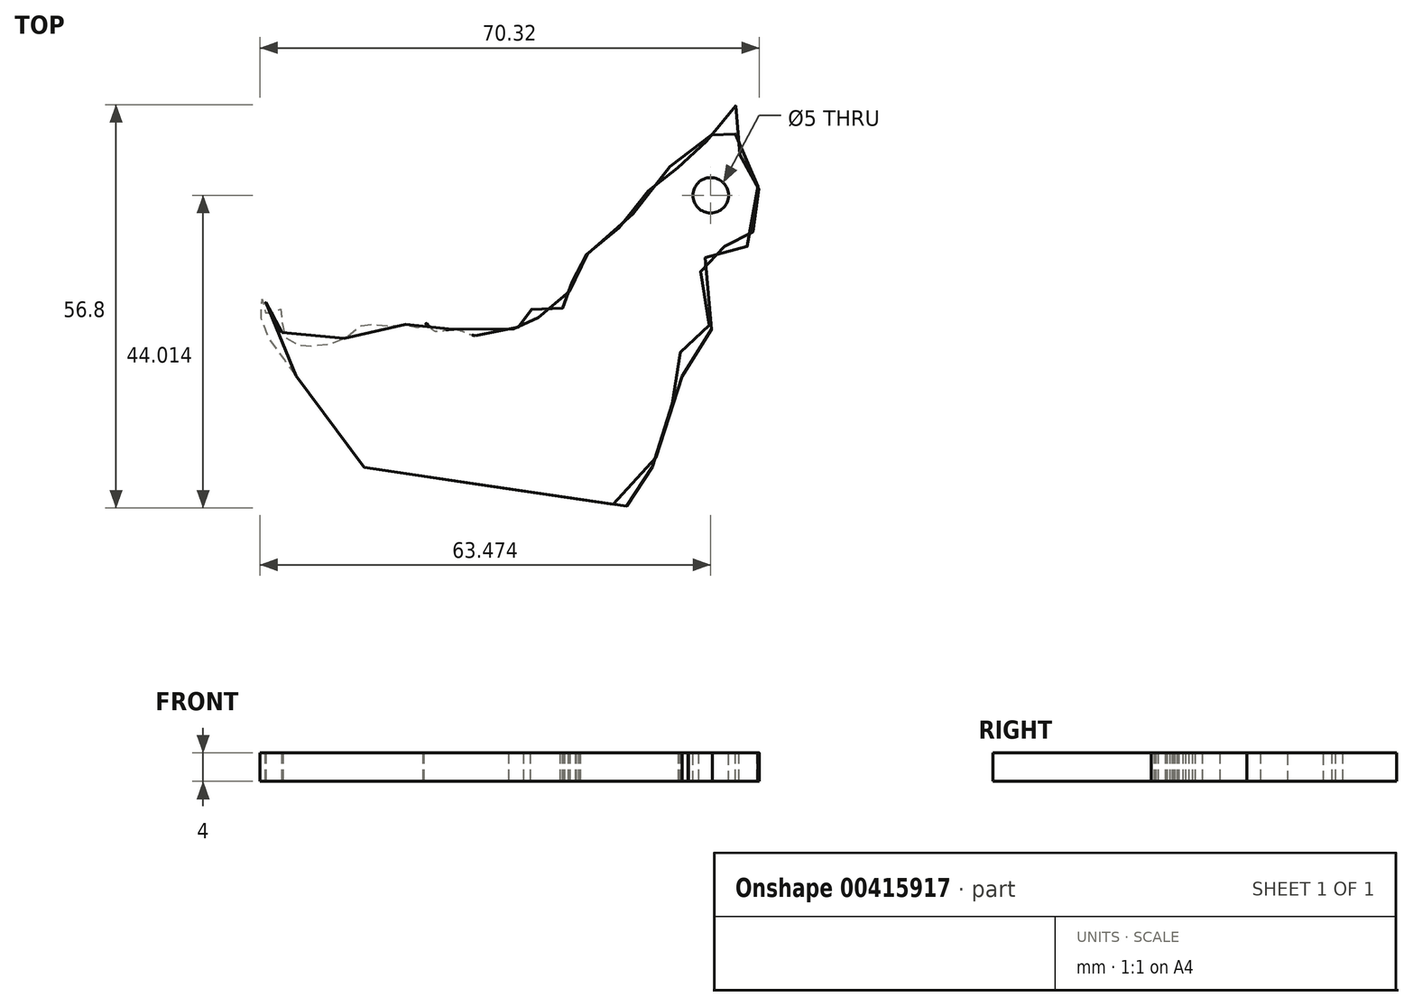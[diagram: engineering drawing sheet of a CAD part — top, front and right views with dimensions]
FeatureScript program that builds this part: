
annotation { "Feature Type Name" : "Feature", "Feature Type Description" : "" }
export const myFeature = defineFeature(function(context is Context, id is Id, definition is map)
    precondition{}
    {
        {
            var Q0;
            Q0=qCreatedBy(makeId("Top.planeOp"),FACE);
            var sketch = newSketch(context, id + "F0", { "sketchPlane" : qUnion([Q0])});
            skLineSegment(sketch, "E0", {"start": v(39.7, 33.45) * mm, "end": v(-31.51, -26.55) * mm, "construction": true});
            skFitSpline(sketch, "E1", {"points": [v(-16.1, -20.73) * mm, v(-17, -19.54) * mm, v(-18.24, -17.94) * mm, v(-19.13, -16.6) * mm, v(-20, -15.45) * mm, v(-21.33, -13.67) * mm, v(-22.36, -12.3) * mm, v(-23.62, -10.56) * mm, v(-24.56, -9.32) * mm, v(-25.25, -8.4) * mm, v(-25.86, -7.54) * mm, v(-26.8, -6.27) * mm, v(-27.74, -4.97) * mm, v(-28.73, -3.62) * mm, v(-29.61, -2.42) * mm, v(-30.16, -1.68) * mm, v(-30.41, -0.5) * mm, v(-30.65, 0.58) * mm, v(-30.76, 1.53) * mm, v(-30.68, 2.53) * mm, v(-30.43, 2.97) * mm, v(-30.1, 2.9) * mm, v(-29.94, 2.3) * mm, v(-29.94, 1.46) * mm, v(-30, 0.9) * mm, v(-30.05, 0.65) * mm, v(-29.8, 0.76) * mm, v(-29.49, 0.96) * mm, v(-29.22, 1.04) * mm, v(-28.9, 1) * mm, v(-28.6, 0.84) * mm, v(-28.5, 0.65) * mm, v(-28.4, 1.15) * mm, v(-28.17, 1.42) * mm, v(-27.85, 1.56) * mm, v(-27.62, 1.32) * mm, v(-27.5, 0.88) * mm, v(-27.5, 0.3) * mm, v(-27.59, -0.23) * mm, v(-27.7, -0.83) * mm, v(-27.7, -1.36) * mm, v(-27.57, -1.87) * mm, v(-27.24, -2.4) * mm, v(-26.8, -2.87) * mm, v(-26.2, -3.25) * mm, v(-25.7, -3.47) * mm, v(-25.37, -3.55) * mm, v(-24.98, -3.42) * mm, v(-24.54, -3.26) * mm, v(-24.1, -3.36) * mm, v(-23.66, -3.55) * mm, v(-23.14, -3.75) * mm, v(-22.55, -3.8) * mm, v(-21.86, -3.64) * mm, v(-20.88, -3.38) * mm, v(-20.22, -3.18) * mm, v(-19.48, -2.84) * mm, v(-18.69, -2.5) * mm, v(-17.99, -2.15) * mm, v(-17.29, -1.67) * mm, v(-16.83, -1.18) * mm, v(-16.34, -0.61) * mm, v(-15.98, -0.42) * mm, v(-15.68, -0.31) * mm, v(-15.41, -0.43) * mm, v(-15.06, -0.58) * mm, v(-14.64, -0.66) * mm, v(-14.16, -0.71) * mm, v(-13.33, -0.78) * mm, v(-12.58, -0.84) * mm, v(-11.78, -0.91) * mm, v(-11.16, -0.9) * mm, v(-10.7, -0.8) * mm, v(-10.29, -0.67) * mm, v(-9.92, -0.6) * mm, v(-9.5, -0.66) * mm, v(-9.11, -0.85) * mm, v(-8.7, -1.02) * mm, v(-8.4, -1.14) * mm, v(-8.13, -1.17) * mm, v(-7.76, -1.11) * mm, v(-7.75, -0.96) * mm, v(-7.81, -0.7) * mm, v(-7.55, -0.6) * mm, v(-7.24, -0.52) * mm, v(-7.02, -0.8) * mm, v(-6.7, -1.16) * mm, v(-6.4, -1.42) * mm, v(-6.04, -1.58) * mm, v(-5.68, -1.61) * mm, v(-5.18, -1.57) * mm, v(-4.78, -1.46) * mm, v(-4.3, -1.37) * mm, v(-3.88, -1.31) * mm, v(-3.25, -1.3) * mm, v(-2.75, -1.42) * mm, v(-2.24, -1.6) * mm, v(-1.76, -1.83) * mm, v(-1.25, -2.02) * mm, v(-0.55, -2.2) * mm, v(-0.14, -2.23) * mm, v(0.2, -2.24) * mm, v(0.83, -2.22) * mm, v(1.42, -2.19) * mm, v(2.14, -2.1) * mm, v(2.8, -2.04) * mm, v(3.44, -2.02) * mm, v(4.05, -2) * mm, v(4.22, -2) * mm, v(4.23, -1.87) * mm, v(4.43, -1.6) * mm, v(4.9, -1.3) * mm, v(5.42, -1.07) * mm, v(5.91, -0.93) * mm, v(6.43, -0.77) * mm, v(6.87, -0.57) * mm, v(7.19, -0.3) * mm, v(7.29, -0.11) * mm, v(7.15, 0.1) * mm, v(6.89, 0.37) * mm, v(6.62, 0.7) * mm, v(6.43, 1.04) * mm, v(6.33, 1.37) * mm, v(6.37, 1.7) * mm, v(6.6, 1.88) * mm, v(6.77, 1.96) * mm, v(7.1, 1.92) * mm, v(7.34, 1.62) * mm, v(7.58, 1.3) * mm, v(7.8, 0.95) * mm, v(8.04, 0.6) * mm, v(8.41, 0.38) * mm, v(8.7, 0.27) * mm, v(8.95, 0.34) * mm, v(9.2, 0.66) * mm, v(9.48, 0.94) * mm, v(9.93, 1.16) * mm, v(10.47, 1.25) * mm, v(11.01, 1.27) * mm, v(11.7, 1.33) * mm, v(12.08, 1.38) * mm, v(11.95, 1.59) * mm, v(11.67, 1.93) * mm, v(11.5, 2.32) * mm, v(11.56, 2.67) * mm, v(11.82, 2.88) * mm, v(11.83, 2.98) * mm, v(11.78, 3.2) * mm, v(11.83, 3.45) * mm, v(11.98, 3.68) * mm, v(12.23, 3.83) * mm, v(12.5, 3.94) * mm, v(12.72, 4.02) * mm, v(12.84, 4.06) * mm, v(12.8, 4.32) * mm, v(12.73, 4.74) * mm, v(12.67, 5.1) * mm, v(12.67, 5.21) * mm, v(13.08, 5.32) * mm, v(13.5, 5.42) * mm, v(13.77, 5.44) * mm, v(13.7, 5.64) * mm, v(13.65, 5.91) * mm, v(13.99, 6.1) * mm, v(14.2, 6.23) * mm, v(14.33, 6.48) * mm, v(14.35, 6.76) * mm, v(14.27, 7.12) * mm, v(14.14, 7.48) * mm, v(14.1, 7.72) * mm, v(14.23, 8.18) * mm, v(14.4, 8.53) * mm, v(14.63, 8.81) * mm, v(14.94, 9.1) * mm, v(15.24, 9.24) * mm, v(15.54, 9.38) * mm, v(15.72, 9.43) * mm, v(15.8, 9.6) * mm, v(15.96, 9.93) * mm, v(16.2, 10.24) * mm, v(16.52, 10.55) * mm, v(16.81, 10.85) * mm, v(17.17, 11.13) * mm, v(17.46, 11.35) * mm, v(18.1, 11.8) * mm, v(18.55, 12.1) * mm, v(18.99, 12.43) * mm, v(19.49, 12.76) * mm, v(20, 13.14) * mm, v(20.32, 13.36) * mm, v(20.96, 13.9) * mm, v(21.36, 14.36) * mm, v(21.63, 14.73) * mm, v(21.82, 15.04) * mm, v(22, 15.35) * mm, v(22.25, 15.83) * mm, v(22.82, 16.3) * mm, v(23.3, 16.72) * mm, v(23.53, 17.25) * mm, v(23.76, 17.76) * mm, v(24.03, 18.35) * mm, v(24.33, 18.74) * mm, v(24.68, 18.94) * mm, v(25.22, 19.15) * mm, v(25.57, 19.39) * mm, v(25.87, 19.63) * mm, v(26.1, 20.13) * mm, v(26.28, 20.7) * mm, v(26.58, 21.29) * mm, v(26.73, 21.7) * mm, v(27.03, 21.55) * mm, v(27.32, 21.26) * mm, v(27.8, 21.26) * mm, v(28.12, 21.52) * mm, v(28.27, 21.94) * mm, v(28.27, 22.38) * mm, v(28.24, 22.68) * mm, v(28.66, 22.74) * mm, v(29.37, 22.83) * mm, v(29.84, 23.24) * mm, v(30.18, 23.83) * mm, v(30.35, 24.15) * mm, v(30.73, 24.48) * mm, v(31.15, 24.68) * mm, v(31.53, 24.8) * mm, v(31.95, 25.02) * mm, v(32.21, 25.27) * mm, v(32.46, 25.6) * mm, v(32.78, 26) * mm, v(33.33, 26.8) * mm, v(33.75, 27.44) * mm, v(34.1, 28.15) * mm, v(34.29, 28.63) * mm, v(34.51, 29.37) * mm, v(34.7, 29.83) * mm, v(35.03, 30.2) * mm, v(35.48, 30.33) * mm, v(36.17, 30.19) * mm, v(36.4, 29.96) * mm, v(36.58, 29.29) * mm, v(36.6, 28.6) * mm, v(36.49, 27.97) * mm, v(36.35, 27.2) * mm, v(36.25, 26.49) * mm, v(36.13, 25.9) * mm, v(36.11, 25.29) * mm, v(36.18, 24.56) * mm, v(36.28, 23.97) * mm, v(36.58, 23.48) * mm, v(37.03, 23.1) * mm, v(37.48, 22.96) * mm, v(38.06, 22.84) * mm, v(38.56, 22.8) * mm, v(38.98, 22.44) * mm, v(39.24, 21.85) * mm, v(39.29, 21) * mm, v(39.18, 20.57) * mm, v(39.14, 20.15) * mm, v(39.15, 19.69) * mm, v(39.25, 19.21) * mm, v(39.36, 18.85) * mm, v(39.48, 18.32) * mm, v(39.55, 17.85) * mm, v(39.56, 17.55) * mm, v(39.56, 16.97) * mm, v(39.53, 16.43) * mm, v(39.46, 15.9) * mm, v(39.39, 15.37) * mm, v(39.4, 14.93) * mm, v(39.37, 14.45) * mm, v(39.38, 13.96) * mm, v(39.35, 13.58) * mm, v(39.2, 13.16) * mm, v(38.94, 12.67) * mm, v(38.61, 12.32) * mm, v(38.33, 11.9) * mm, v(38.2, 11.65) * mm, v(37.91, 10.81) * mm, v(37.8, 10.22) * mm, v(37.65, 9.87) * mm, v(37.3, 9.49) * mm, v(36.95, 9.32) * mm, v(36.53, 9.25) * mm, v(36.08, 9.3) * mm, v(35.65, 9.5) * mm, v(35.26, 9.81) * mm, v(34.89, 10.15) * mm, v(34.58, 10.48) * mm, v(34.22, 10.82) * mm, v(33.91, 11.06) * mm, v(33.56, 11.15) * mm, v(33.2, 11.02) * mm, v(32.91, 10.73) * mm, v(32.61, 10.26) * mm, v(32.35, 9.66) * mm, v(32.16, 9.28) * mm, v(31.9, 8.67) * mm, v(31.7, 8.16) * mm, v(31.5, 7.55) * mm, v(31.33, 7) * mm, v(31.18, 6.42) * mm, v(31.08, 5.9) * mm, v(30.94, 5.02) * mm, v(30.97, 4.33) * mm, v(30.94, 3.62) * mm, v(31.02, 2.8) * mm, v(31.34, 1.9) * mm, v(31.76, 0.88) * mm, v(32.05, 0.28) * mm, v(32.32, -0.31) * mm, v(32.7, -1.08) * mm, v(32.9, -1.66) * mm, v(32.8, -2.6) * mm, v(32.38, -3.19) * mm, v(31.67, -3.6) * mm, v(30.93, -3.87) * mm, v(30.09, -4.07) * mm, v(29.54, -4.16) * mm, v(29.58, -3.79) * mm, v(29.28, -3.93) * mm, v(28.71, -4.31) * mm, v(28.24, -4.8) * mm, v(28.1, -5.6) * mm, v(28.23, -6.45) * mm, v(28.5, -7.08) * mm, v(28.65, -7.61) * mm, v(28.68, -8.19) * mm, v(28.6, -8.82) * mm, v(28.42, -9.46) * mm, v(28.14, -10.06) * mm, v(27.78, -10.88) * mm, v(27.27, -11.79) * mm, v(26.8, -12.74) * mm, v(26.25, -13.87) * mm, v(25.76, -15) * mm, v(25.43, -15.85) * mm, v(25.32, -16.97) * mm, v(25.28, -18.1) * mm, v(25.13, -18.95) * mm, v(24.68, -20.14) * mm, v(24.3, -21.23) * mm, v(24.08, -22.46) * mm, v(23.97, -23.56) * mm, v(23.84, -24.12) * mm, v(23.63, -24.83) * mm, v(23.38, -25.49) * mm, v(23.03, -26.09) * mm, v(22.68, -26.45) * mm, v(22.18, -26.4) * mm, v(21.57, -26.3) * mm, v(20.78, -26.19) * mm, v(19.87, -26.06) * mm, v(19.24, -25.97) * mm, v(15.9, -25.48) * mm, v(13.9, -25.2) * mm, v(11.32, -24.78) * mm, v(8.85, -24.42) * mm, v(6.35, -24.07) * mm, v(3.68, -23.69) * mm, v(2.26, -23.45) * mm, v(0.47, -23.22) * mm, v(-1.15, -22.98) * mm, v(-2.33, -22.8) * mm, v(-3.98, -22.55) * mm, v(-5.48, -22.34) * mm, v(-6.99, -22.07) * mm, v(-8.94, -21.8) * mm, v(-12.3, -21.33) * mm, v(-13.9, -21.08) * mm, v(-15.26, -20.86) * mm, v(-16.1, -20.73) * mm]});
            skSolve(sketch);
        }
        {
            var Q0;
            Q0=makeQuery(id+"F0.imprint","IMPRINT",FACE,{"disambiguationData":[TD([[makeQuery(id+"F0.imprint","IMPRINT",EDGE,{"derivedFrom":sQuery(id+"F0.wireOp",EDGE,"E1")}),-1.0]])]});
            extrude(context, id + "F1", {"entities" : qUnion([Q0]), "depth" : 4 * mm});
        }
        {
            var Q0;
            Q0=makeQuery(id+"F1.opExtrude","CAP_FACE",FACE,{"disambiguationData":[OSD([sQuery(id+"F0.wireOp",EDGE,"E1")])],"isStart":false});
            var sketch = newSketch(context, id + "F2", { "sketchPlane" : qUnion([Q0])});
            skCircle(sketch, "E2", {"center": v(32.71, 17.54) * mm, "radius": 2.5 * mm});
            skSolve(sketch);
        }
        {
            var Q0;
            Q0=makeQuery(id+"F2.imprint","IMPRINT",FACE,{"disambiguationData":[TD([[makeQuery(id+"F2.imprint","IMPRINT",EDGE,{"derivedFrom":sQuery(id+"F2.wireOp",EDGE,"E2")}),1.0]])]});
            extrude(context, id + "F3", {"entities" : qUnion([Q0]), "operationType" : NewBodyOperationType.REMOVE, "oppositeDirection" : true, "depth" : 25 * mm});
        }
    });
